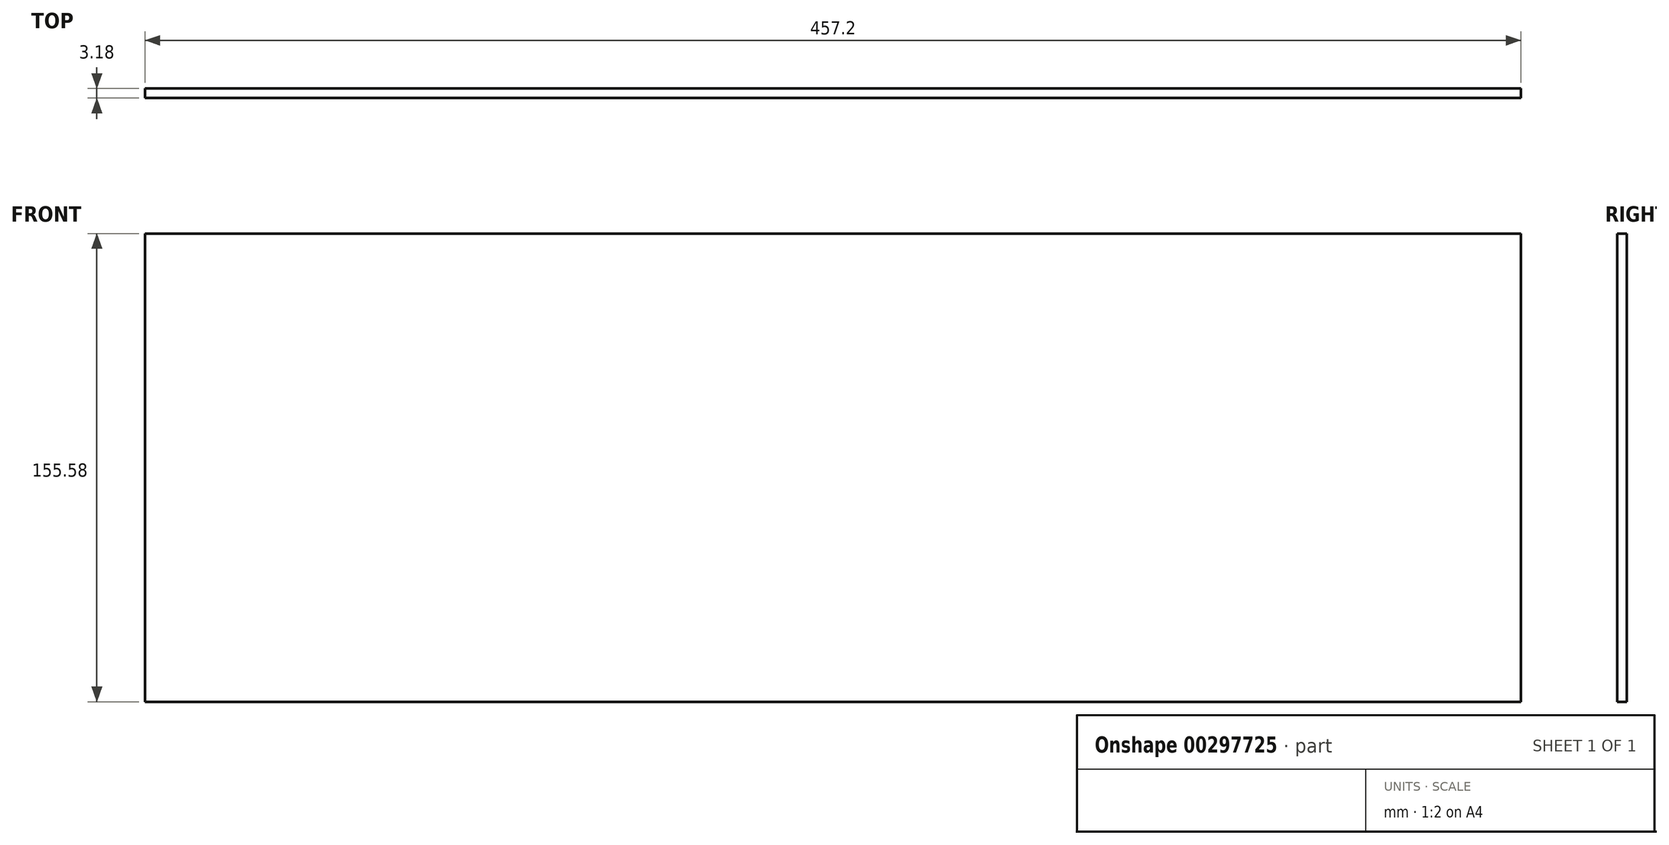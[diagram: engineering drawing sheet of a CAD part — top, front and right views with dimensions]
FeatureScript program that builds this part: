
annotation { "Feature Type Name" : "Feature", "Feature Type Description" : "" }
export const myFeature = defineFeature(function(context is Context, id is Id, definition is map)
    precondition{}
    {
        {
            var Q0;
            Q0=qCreatedBy(makeId("Front.planeOp"),FACE);
            var sketch = newSketch(context, id + "F0", { "sketchPlane" : qUnion([Q0])});
            skLineSegment(sketch, "E0.bottom", {"start": v(228.6, -77.79) * mm, "end": v(-228.6, -77.79) * mm});
            skLineSegment(sketch, "E0.top", {"start": v(228.6, 77.79) * mm, "end": v(-228.6, 77.79) * mm});
            skLineSegment(sketch, "E0.left", {"start": v(228.6, -77.79) * mm, "end": v(228.6, 77.79) * mm});
            skLineSegment(sketch, "E0.right", {"start": v(-228.6, -77.79) * mm, "end": v(-228.6, 77.79) * mm});
            skPoint(sketch, "E0.middle", {"position": v(0, 0) * mm});
            skSolve(sketch);
        }
        {
            var Q0;
            Q0 = qSketchRegion(id + "F0", true);
            extrude(context, id + "F1", {"entities" : qUnion([Q0]), "endBound" : BoundingType.SYMMETRIC, "depth" : 3.17 * mm});
        }
    });
